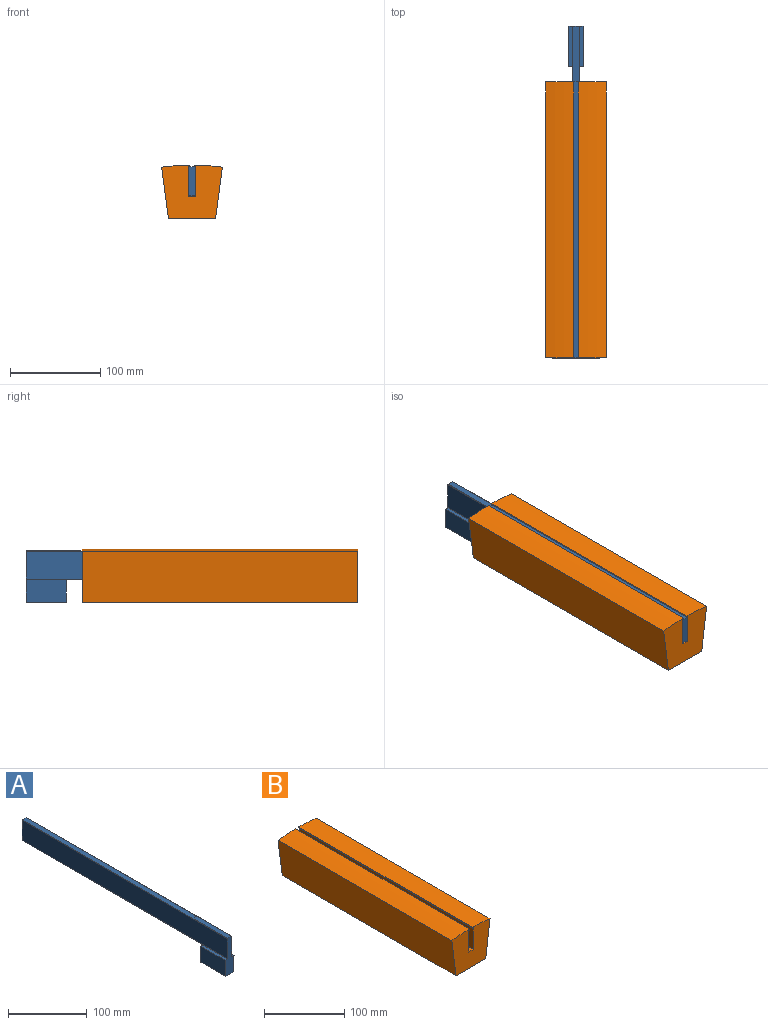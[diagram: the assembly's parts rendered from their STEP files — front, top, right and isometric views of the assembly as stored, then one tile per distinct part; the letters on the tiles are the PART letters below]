
ASSEMBLY  parts=2 mates=1
PART A: 17 faces, bbox 15.7x368.3x57.2 mm
  f0: plane 306.2x7.16mm, normal (0,0,1), area 2193.2mm2, adj f2,f3,f4,f10
  f1: plane 368.3x30.99mm, normal (1,0,0), area 11412.9mm2, adj f2,f8,f9,f10
  f2: cylinder r=0.38mm len=368.3mm, axis (0,1,0), area 220.4mm2, adj f0,f1,f3,f9,f10
  f3: plane 62.1x7.16mm, normal (0,0,1), area 444.8mm2, adj f0,f2,f4,f9
  f4: cylinder r=0.38mm len=368.3mm, axis (0,1,0), area 220.4mm2, adj f0,f3,f5,f9,f10
  f5: plane 368.3x30.99mm, normal (-1,0,0), area 11412.9mm2, adj f4,f6,f9,f10
  f6: cylinder r=0.38mm len=368.3mm, axis (0,1,0), area 220.4mm2, adj f5,f7,f9,f10,f11
  f7: plane 323.85x7.16mm, normal (0,0,-1), area 2319.7mm2, adj f6,f8,f10,f16
  f8: cylinder r=0.38mm len=368.3mm, axis (0,1,0), area 220.4mm2, adj f1,f7,f9,f10,f15
  f9: plane 57.24x15.68mm, normal (0,-1,0), area 627.2mm2, adj f1,f2,f3,f4,f5,f6,f8,f11
  f10: plane 31.75x7.93mm, normal (0,1,0), area 251.5mm2, adj f0,f1,f2,f4,f5,f6,f7,f8
  f11: cylinder r=224.67mm len=44.45mm, axis (0,-1,0), area 189.4mm2, adj f6,f9,f12,f16
  f12: plane 44.45x25.38mm, normal (-1,0,-0.03), area 1129mm2, adj f9,f11,f13,f16
  f13: cylinder r=199.27mm len=44.45mm, axis (0,-1,0), area 618.4mm2, adj f9,f12,f14,f16
  f14: plane 44.45x25.38mm, normal (1,0,-0.03), area 1129mm2, adj f9,f13,f15,f16
  f15: cylinder r=224.67mm len=44.45mm, axis (0,-1,0), area 189.4mm2, adj f8,f9,f14,f16
  f16: plane 25.49x15.68mm, normal (0,1,0), area 375.7mm2, adj f7,f11,f12,f13,f14,f15
PART B: 20 faces, bbox 67.3x306.2x59.5 mm
  f0: cylinder r=0.25mm len=306.2mm, axis (0,1,0), area 120.2mm2, adj f1,f17,f18,f19
  f1: plane 306.2x32.52mm, normal (1,0,0), area 9957.5mm2, adj f0,f2,f18,f19
  f2: cylinder r=0.25mm len=306.2mm, axis (0,1,0), area 120.2mm2, adj f1,f3,f18,f19
  f3: plane 306.2x1mm, normal (0,0,-1), area 305.8mm2, adj f2,f4,f18,f19
  f4: cylinder r=0.25mm len=306.2mm, axis (0,1,0), area 120.2mm2, adj f3,f5,f18,f19
  f5: plane 306.2x1.25mm, normal (1,0,0), area 382mm2, adj f4,f6,f18,f19
  f6: cylinder r=257.9mm len=306.2mm, axis (0,1,0), area 9524.1mm2, adj f5,f7,f18,f19
  f7: plane 306.2x57.33mm, normal (-0.99,0,-0.13), area 17704.2mm2, adj f6,f8,f18,f19
  f8: plane 306.2x52.23mm, normal (0,0,-1), area 15993mm2, adj f7,f9,f18,f19
  f9: plane 306.2x57.33mm, normal (0.99,0,-0.13), area 17704.2mm2, adj f8,f10,f18,f19
  f10: cylinder r=257.9mm len=306.2mm, axis (0,1,0), area 9524.1mm2, adj f9,f11,f18,f19
  f11: plane 306.2x1.25mm, normal (-1,0,0), area 382mm2, adj f10,f12,f18,f19
  f12: cylinder r=0.25mm len=306.2mm, axis (0,1,0), area 120.2mm2, adj f11,f13,f18,f19
  f13: plane 306.2x1mm, normal (0,0,-1), area 305.8mm2, adj f12,f14,f18,f19
  f14: cylinder r=0.25mm len=306.2mm, axis (0,1,0), area 120.2mm2, adj f13,f15,f18,f19
  f15: plane 306.2x32.52mm, normal (-1,0,0), area 9957.5mm2, adj f14,f16,f18,f19
  f16: cylinder r=0.25mm len=306.2mm, axis (0,1,0), area 120.2mm2, adj f15,f17,f18,f19
  f17: plane 306.2x7.81mm, normal (0,0,1), area 2390.1mm2, adj f0,f16,f18,f19
  f18: plane 67.33x59.52mm, normal (0,-1,0), area 3243.7mm2, adj f0,f1,f2,f3,f4,f5,f6,f7
  f19: plane 67.33x59.52mm, normal (0,1,0), area 3243.7mm2, adj f0,f1,f2,f3,f4,f5,f6,f7
PLACE A rot(axis=(0,0,1),180deg) t=(0,0,-0.27)mm
PLACE B t=(0,306.2,0)mm
MATE fastened A.f10 <-> B.f18  axis (0,-1,0) through (0,0,224.37)mm
